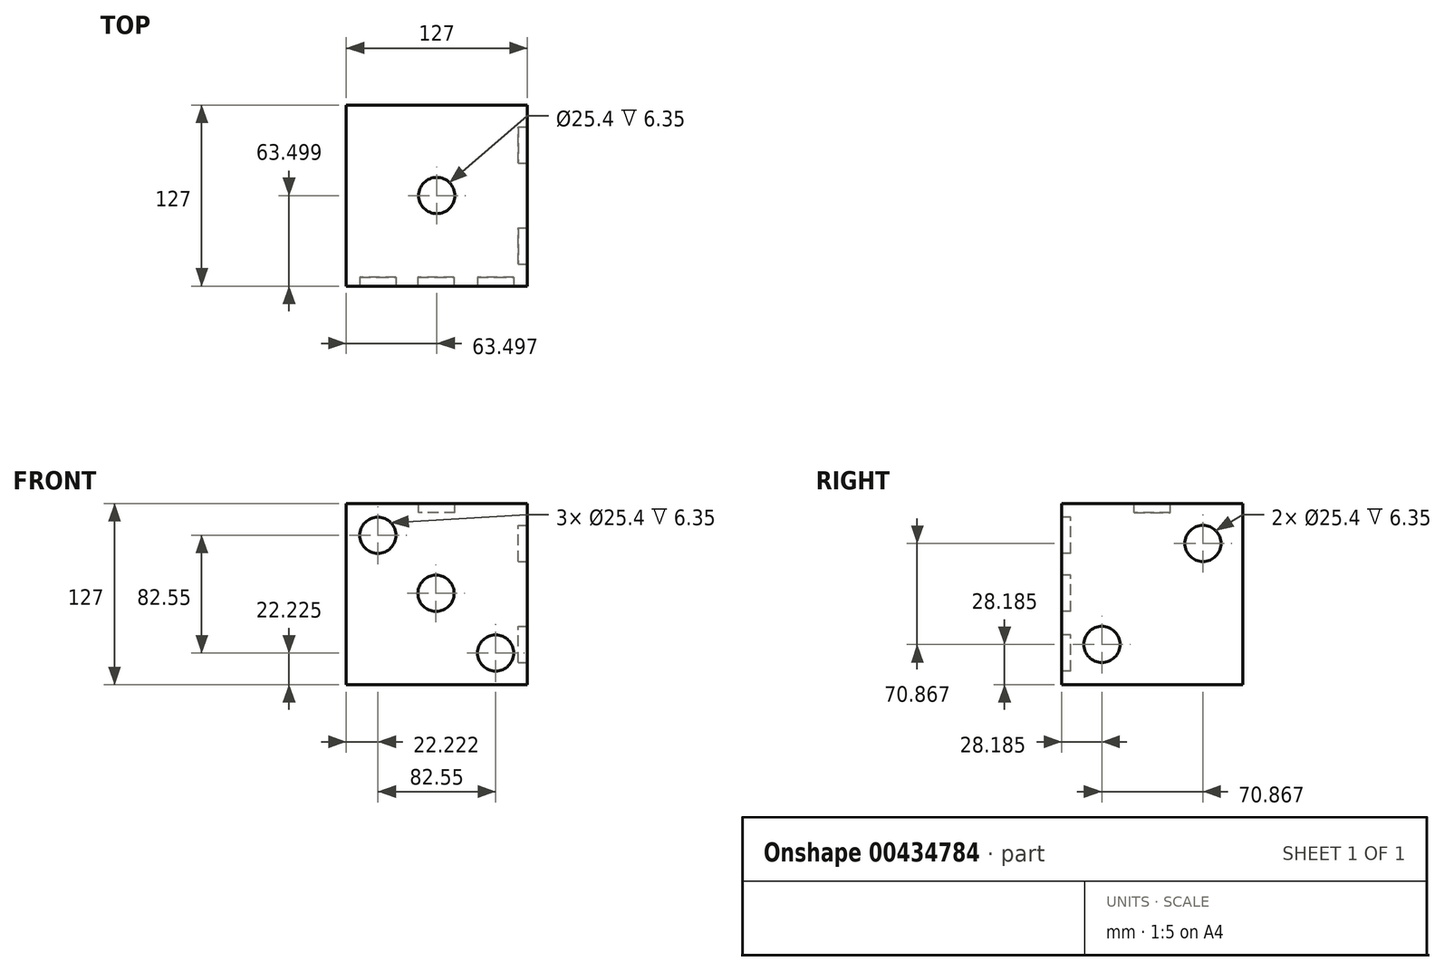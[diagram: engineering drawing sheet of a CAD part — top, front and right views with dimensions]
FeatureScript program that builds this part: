
annotation { "Feature Type Name" : "Feature", "Feature Type Description" : "" }
export const myFeature = defineFeature(function(context is Context, id is Id, definition is map)
    precondition{}
    {
        {
            var Q0;
            Q0=qCreatedBy(makeId("Top.planeOp"),FACE);
            var sketch = newSketch(context, id + "F0", { "sketchPlane" : qUnion([Q0])});
            skLineSegment(sketch, "E0.bottom", {"start": v(-62.95, 74.68) * mm, "end": v(64.05, 74.68) * mm});
            skLineSegment(sketch, "E0.top", {"start": v(-62.95, -52.32) * mm, "end": v(64.05, -52.32) * mm});
            skLineSegment(sketch, "E0.left", {"start": v(-62.95, 74.68) * mm, "end": v(-62.95, -52.32) * mm});
            skLineSegment(sketch, "E0.right", {"start": v(64.05, 74.68) * mm, "end": v(64.05, -52.32) * mm});
            skSolve(sketch);
        }
        {
            var Q0;
            Q0 = qSketchRegion(id + "F0", true);
            extrude(context, id + "F1", {"entities" : qUnion([Q0]), "depth" : 127 * mm});
        }
        {
            var Q0;
            Q0=makeQuery(id+"F1.opExtrude","CAP_FACE",FACE,{"disambiguationData":[OSD([sQuery(id+"F0.wireOp",EDGE,"E0.bottom"),sQuery(id+"F0.wireOp",EDGE,"E0.top"),sQuery(id+"F0.wireOp",EDGE,"E0.left"),sQuery(id+"F0.wireOp",EDGE,"E0.right")])],"isStart":false});
            var sketch = newSketch(context, id + "F2", { "sketchPlane" : qUnion([Q0])});
            skCircle(sketch, "E1", {"center": v(0.55, 11.18) * mm, "radius": 12.7 * mm});
            skPoint(sketch, "E1.centerSnap0", {"position": v(64.05, 11.18) * mm});
            skPoint(sketch, "E1.centerSnap1", {"position": v(0.55, 74.68) * mm});
            skSolve(sketch);
        }
        {
            var Q0;
            Q0 = qSketchRegion(id + "F2", true);
            extrude(context, id + "F3", {"entities" : qUnion([Q0]), "operationType" : NewBodyOperationType.REMOVE, "oppositeDirection" : true, "depth" : 6.35 * mm});
        }
        {
            var Q0;
            Q0=makeQuery(id+"F1.opExtrude","SWEPT_FACE",FACE,{"disambiguationData":[OSD([sQuery(id+"F0.wireOp",EDGE,"E0.right")])]});
            var sketch = newSketch(context, id + "F4", { "sketchPlane" : qUnion([Q0])});
            skLineSegment(sketch, "E2", {"start": v(74.68, 127) * mm, "end": v(-52.32, 0) * mm, "construction": true});
            skCircle(sketch, "E3", {"center": v(46.73, 99.05) * mm, "radius": 12.7 * mm});
            skCircle(sketch, "E4", {"center": v(-24.14, 28.19) * mm, "radius": 12.7 * mm});
            skSolve(sketch);
        }
        {
            var Q0;
            Q0 = qSketchRegion(id + "F4", true);
            extrude(context, id + "F5", {"entities" : qUnion([Q0]), "operationType" : NewBodyOperationType.ADD, "oppositeDirection" : true, "depth" : 6.35 * mm});
        }
        {
            var Q0;
            Q0 = qSketchRegion(id + "F4", true);
            extrude(context, id + "F6", {"entities" : qUnion([Q0]), "operationType" : NewBodyOperationType.REMOVE, "oppositeDirection" : true, "depth" : 6.35 * mm});
        }
        {
            var Q0;
            Q0=makeQuery(id+"F1.opExtrude","SWEPT_FACE",FACE,{"disambiguationData":[OSD([sQuery(id+"F0.wireOp",EDGE,"E0.top")])]});
            var sketch = newSketch(context, id + "F7", { "sketchPlane" : qUnion([Q0])});
            skLineSegment(sketch, "E5", {"start": v(-62.95, 127) * mm, "end": v(64.05, 0) * mm, "construction": true});
            skCircle(sketch, "E6", {"center": v(-40.73, 104.78) * mm, "radius": 12.7 * mm});
            skCircle(sketch, "E7", {"center": v(0, 64.05) * mm, "radius": 12.7 * mm});
            skCircle(sketch, "E8", {"center": v(41.82, 22.23) * mm, "radius": 12.7 * mm});
            skSolve(sketch);
        }
        {
            var Q0;
            Q0 = qSketchRegion(id + "F7", true);
            extrude(context, id + "F8", {"entities" : qUnion([Q0]), "operationType" : NewBodyOperationType.REMOVE, "oppositeDirection" : true, "depth" : 6.35 * mm});
        }
    });
